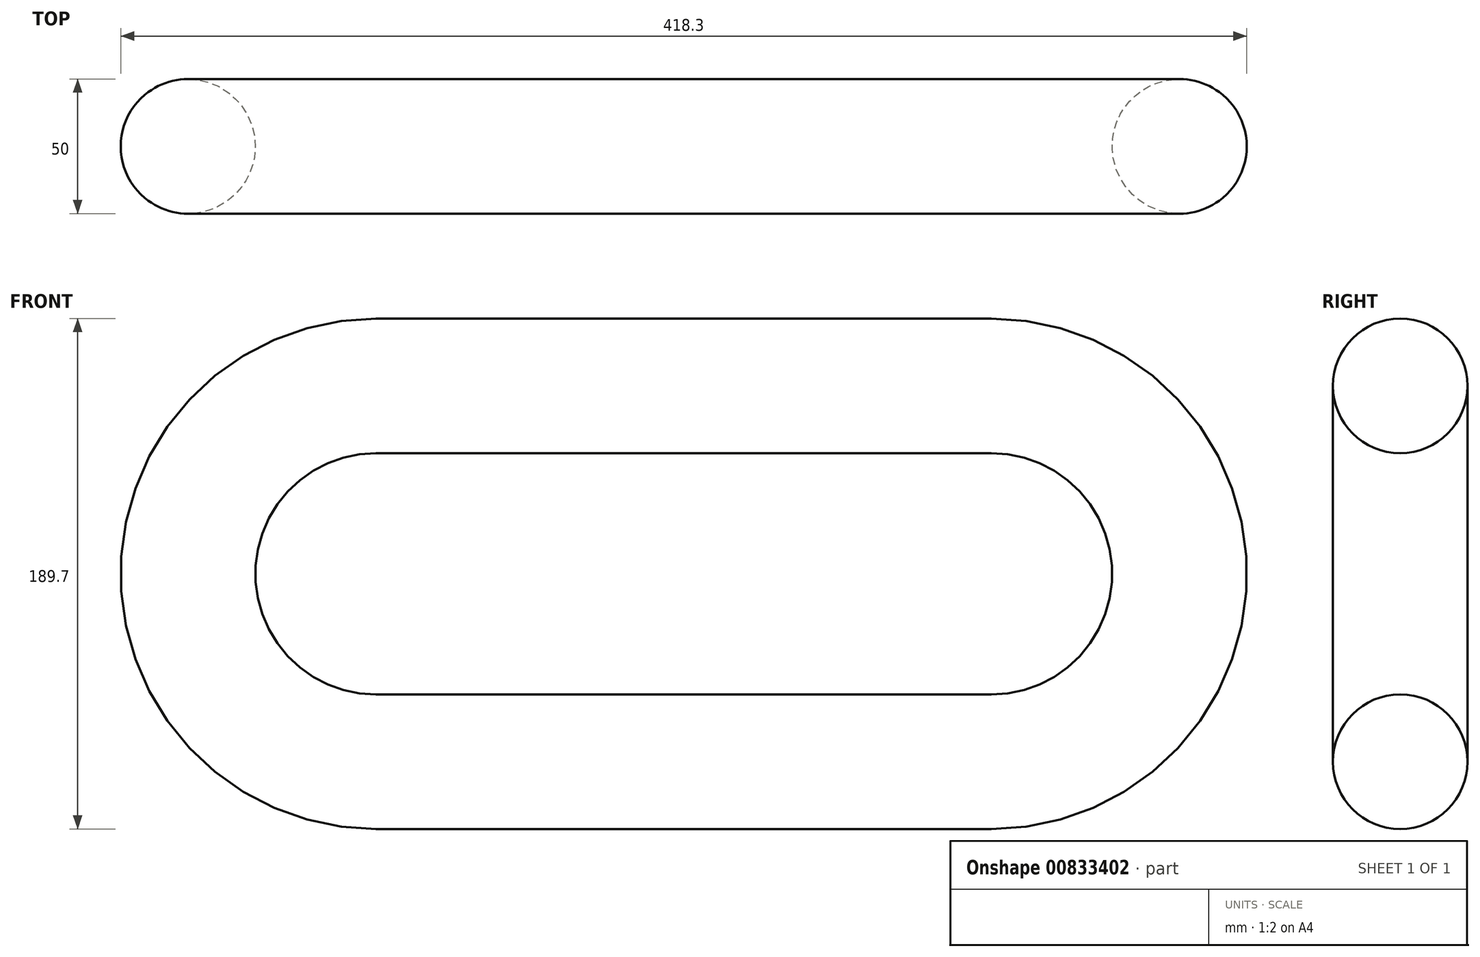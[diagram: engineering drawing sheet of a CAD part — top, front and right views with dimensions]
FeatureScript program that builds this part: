
annotation { "Feature Type Name" : "Feature", "Feature Type Description" : "" }
export const myFeature = defineFeature(function(context is Context, id is Id, definition is map)
    precondition{}
    {
        {
            var Q0;
            Q0=qCreatedBy(makeId("Front.planeOp"),FACE);
            var sketch = newSketch(context, id + "F0", { "sketchPlane" : qUnion([Q0])});
            skLineSegment(sketch, "E0", {"start": v(0, 0) * mm, "end": v(114.3, 0) * mm});
            skLineSegment(sketch, "E1", {"start": v(0, 0) * mm, "end": v(-114.3, 0) * mm});
            skLineSegment(sketch, "E2", {"start": v(-114.3, 0) * mm, "end": v(-114.3, 139.7) * mm});
            skLineSegment(sketch, "E3", {"start": v(114.3, 0) * mm, "end": v(114.3, 139.7) * mm});
            skArc(sketch, "E4", {"start": v(-114.3, 139.7) * mm, "mid": v(-184.15, 69.85) * mm, "end": v(-114.3, 0) * mm});
            skArc(sketch, "E5", {"start": v(114.3, 0) * mm, "mid": v(184.15, 69.85) * mm, "end": v(114.3, 139.7) * mm});
            skLineSegment(sketch, "E6", {"start": v(-114.3, 139.7) * mm, "end": v(114.3, 139.7) * mm});
            skSolve(sketch);
        }
        {
            var Q0;
            Q0=qCreatedBy(makeId("Right.planeOp"),FACE);
            var sketch = newSketch(context, id + "F1", { "sketchPlane" : qUnion([Q0])});
            skCircle(sketch, "E7", {"center": v(0, 0) * mm, "radius": 25 * mm});
            skSolve(sketch);
        }
        {
            var Q0;
            Q0=makeQuery(id+"F1.imprint","IMPRINT",FACE,{"disambiguationData":[TD([[makeQuery(id+"F1.imprint","IMPRINT",EDGE,{"derivedFrom":sQuery(id+"F1.wireOp",EDGE,"E7")}),1.0]])]});
            var Q1;
            Q1=sQuery(id+"F0.wireOp",EDGE,"E1");
            var Q2;
            Q2=sQuery(id+"F0.wireOp",EDGE,"E4");
            var Q3;
            Q3=sQuery(id+"F0.wireOp",EDGE,"E6");
            var Q4;
            Q4=sQuery(id+"F0.wireOp",EDGE,"E5");
            var Q5;
            Q5=sQuery(id+"F0.wireOp",EDGE,"E0");
            sweep(context, id + "F2", {"profiles" : qUnion([Q0]), "path" : qUnion([Q1, Q2, Q3, Q4, Q5])});
        }
    });
